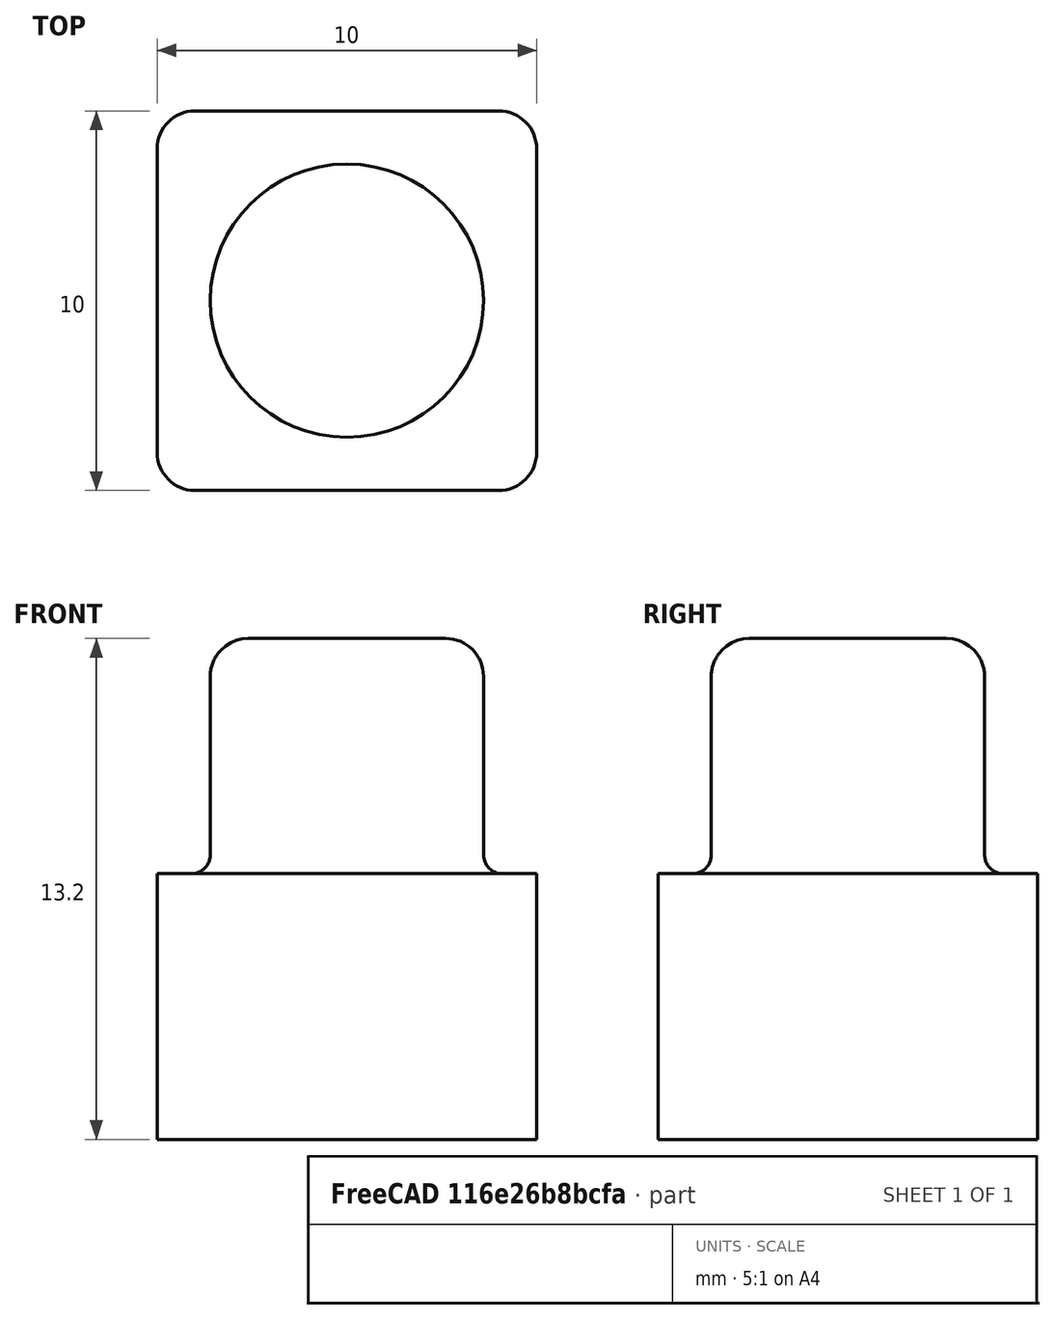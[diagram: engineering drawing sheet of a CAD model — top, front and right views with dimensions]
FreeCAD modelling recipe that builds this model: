
FCSTD DOCUMENT  (FreeCAD 0.18R16146 (Git))
Label: Foot 0.1
License: All rights reserved
LicenseURL: http://en.wikipedia.org/wiki/All_rights_reserved
objects: Part::Fillet×3, Part::Cylinder×1, Part::Box×1, Part::MultiFuse×1
note: 6 computed .brp shape members not serialized (recipe doc carries the construction recipe); baked Part::Feature solids carry a one-line shape summary decoded from their .brp

FEATURE [Part::Cylinder] Cylinder
  Angle = 360
  AttacherType = Attacher::AttachEngine3D
  Height = 6.2
  Radius = 3.6
FEATURE [Part::Box] Box  label="Cube"
  AttacherType = Attacher::AttachEngine3D
  Height = 7
  Length = 10
  Placement = pos=(-5,-5,-7) rot=(0,0,1;0rad)
  Width = 10
FEATURE [Part::MultiFuse] Fusion
  Shapes = -> [Box,Cylinder]
FEATURE [Part::Fillet] Fillet
  Base = -> Fusion
  Edges = 4 edges r=1: [Edge1,Edge3,Edge6,Edge12]
FEATURE [Part::Fillet] Fillet001
  Base = -> Fillet
  Edges = 1 edges r=0.5: [Edge12]
FEATURE [Part::Fillet] Fillet002
  Base = -> Fillet001
  Edges = 1 edges r=1: [Edge29]
